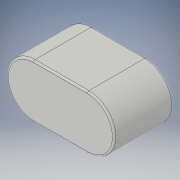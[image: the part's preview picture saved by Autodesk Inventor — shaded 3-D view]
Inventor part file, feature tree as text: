
AUTODESK INVENTOR PART (.ipt)
format: ipt  version: 2019.4 (Build 234330000, 330)  size: 124,928 bytes
history: native  units: mm
features: other x1, extrude x1, fillet x1, sketch x1
ambient origin geometry x8: Origin, YZ Plane, XZ Plane, XY Plane, X Axis, Y Axis, Z Axis, Center Point
bodies: Body1 (feature_tree)
feature tree (4):
  other  "實體1"
  extrude  "擠出1"  Depth=5.0mm
  fillet  "圓角1"  Radius=5.0mm
  sketch  "草圖1"
